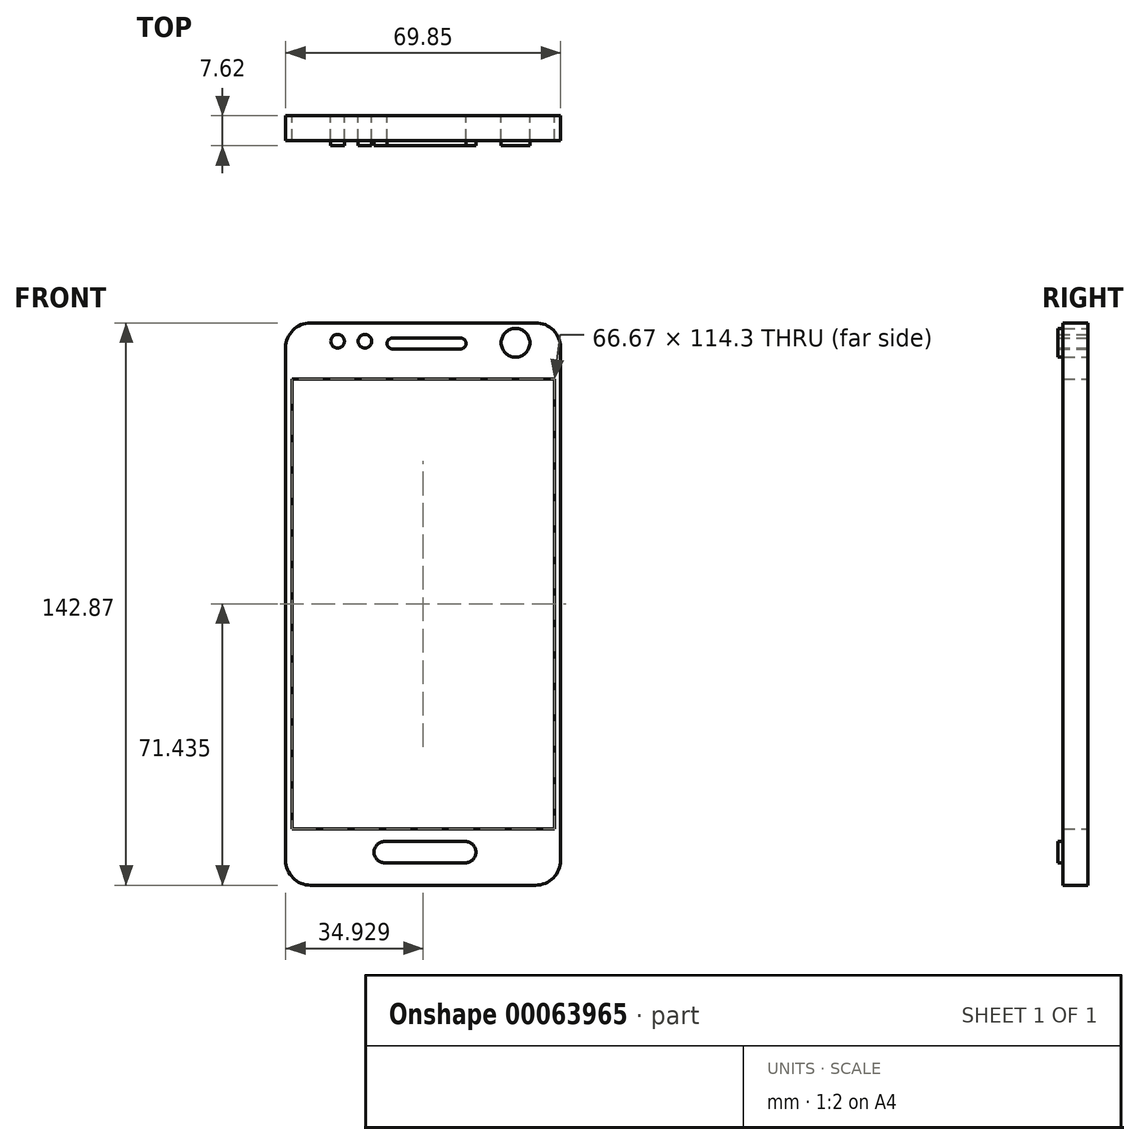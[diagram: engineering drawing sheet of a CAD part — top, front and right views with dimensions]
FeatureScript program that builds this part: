
annotation { "Feature Type Name" : "Feature", "Feature Type Description" : "" }
export const myFeature = defineFeature(function(context is Context, id is Id, definition is map)
    precondition{}
    {
        {
            var Q0;
            Q0=qCreatedBy(makeId("Front.planeOp"),FACE);
            var sketch = newSketch(context, id + "F0", { "sketchPlane" : qUnion([Q0])});
            skLineSegment(sketch, "E0.bottom", {"start": v(-34.08, 123.22) * mm, "end": v(23.07, 123.22) * mm});
            skLineSegment(sketch, "E0.top", {"start": v(-34.08, -19.65) * mm, "end": v(23.07, -19.65) * mm});
            skLineSegment(sketch, "E0.left", {"start": v(-40.43, 116.87) * mm, "end": v(-40.43, -13.3) * mm});
            skLineSegment(sketch, "E0.right", {"start": v(29.42, 116.87) * mm, "end": v(29.42, -13.3) * mm});
            skPoint(sketch, "E1.visualSharp", {"position": v(-40.43, 123.22) * mm});
            skArc(sketch, "E1.filletArc", {"start": v(-34.08, 123.22) * mm, "mid": v(-38.57, 121.36) * mm, "end": v(-40.43, 116.87) * mm});
            skPoint(sketch, "E2.visualSharp", {"position": v(29.42, 123.22) * mm});
            skArc(sketch, "E2.filletArc", {"start": v(29.42, 116.87) * mm, "mid": v(27.56, 121.36) * mm, "end": v(23.07, 123.22) * mm});
            skPoint(sketch, "E3.visualSharp", {"position": v(-40.43, -19.65) * mm});
            skArc(sketch, "E3.filletArc", {"start": v(-40.43, -13.3) * mm, "mid": v(-38.57, -17.8) * mm, "end": v(-34.08, -19.65) * mm});
            skPoint(sketch, "E4.visualSharp", {"position": v(29.42, -19.65) * mm});
            skArc(sketch, "E4.filletArc", {"start": v(23.07, -19.65) * mm, "mid": v(27.56, -17.8) * mm, "end": v(29.42, -13.3) * mm});
            skLineSegment(sketch, "E5.0", {"start": v(-38.84, 108.93) * mm, "end": v(27.84, 108.93) * mm});
            skLineSegment(sketch, "E6.0", {"start": v(-38.84, -5.37) * mm, "end": v(27.84, -5.37) * mm});
            skLineSegment(sketch, "E7.0", {"start": v(-38.84, 108.93) * mm, "end": v(-38.84, -5.37) * mm});
            skLineSegment(sketch, "E8.0", {"start": v(27.84, 108.93) * mm, "end": v(27.84, -5.37) * mm});
            skSolve(sketch);
        }
        {
            var Q0;
            Q0 = qSketchRegion(id + "F0", true);
            extrude(context, id + "F1", {"entities" : qUnion([Q0]), "depth" : 6.35 * mm});
        }
        {
            var Q0;
            Q0=qCreatedBy(makeId("Front.planeOp"),FACE);
            var sketch = newSketch(context, id + "F2", { "sketchPlane" : qUnion([Q0])});
            skLineSegment(sketch, "E9", {"start": v(-15.26, -8.55) * mm, "end": v(5.22, -8.55) * mm});
            skLineSegment(sketch, "E10", {"start": v(5.22, -8.55) * mm, "end": v(5.22, -13.96) * mm});
            skLineSegment(sketch, "E11", {"start": v(5.22, -13.96) * mm, "end": v(-15.26, -13.96) * mm});
            skLineSegment(sketch, "E12", {"start": v(-15.26, -13.96) * mm, "end": v(-15.26, -8.55) * mm});
            skArc(sketch, "E13", {"start": v(-15.26, -8.55) * mm, "mid": v(-17.96, -11.26) * mm, "end": v(-15.26, -13.96) * mm});
            skArc(sketch, "E14", {"start": v(5.22, -13.96) * mm, "mid": v(7.92, -11.26) * mm, "end": v(5.22, -8.55) * mm});
            skSolve(sketch);
        }
        {
            var Q0;
            Q0 = qSketchRegion(id + "F2", true);
            extrude(context, id + "F3", {"entities" : qUnion([Q0]), "operationType" : NewBodyOperationType.ADD, "depth" : 7.62 * mm});
        }
        {
            var Q0;
            Q0=qCreatedBy(makeId("Front.planeOp"),FACE);
            var sketch = newSketch(context, id + "F4", { "sketchPlane" : qUnion([Q0])});
            skCircle(sketch, "E15", {"center": v(-20.28, 118.55) * mm, "radius": 1.73 * mm});
            skLineSegment(sketch, "E16", {"start": v(-23.76, 123.57) * mm, "end": v(-23.76, 77.98) * mm, "construction": true});
            skCircle(sketch, "E17.MirrorC", {"center": v(-27.24, 118.55) * mm, "radius": 1.73 * mm});
            skLineSegment(sketch, "E18.bottom", {"start": v(-13.33, 119.32) * mm, "end": v(4.06, 119.32) * mm});
            skLineSegment(sketch, "E18.top", {"start": v(-13.33, 116.62) * mm, "end": v(4.06, 116.62) * mm});
            skLineSegment(sketch, "E18.left", {"start": v(-13.33, 119.32) * mm, "end": v(-13.33, 116.62) * mm});
            skLineSegment(sketch, "E18.right", {"start": v(4.06, 119.32) * mm, "end": v(4.06, 116.62) * mm});
            skArc(sketch, "E19", {"start": v(4.06, 116.62) * mm, "mid": v(5.4, 117.97) * mm, "end": v(4.06, 119.32) * mm});
            skArc(sketch, "E20", {"start": v(-13.33, 119.32) * mm, "mid": v(-14.68, 117.97) * mm, "end": v(-13.33, 116.62) * mm});
            skCircle(sketch, "E21", {"center": v(17.96, 118.16) * mm, "radius": 3.64 * mm});
            skSolve(sketch);
        }
        {
            var Q0;
            Q0 = qSketchRegion(id + "F4", true);
            extrude(context, id + "F5", {"entities" : qUnion([Q0]), "depth" : 7.62 * mm});
        }
    });
